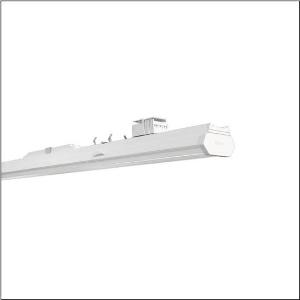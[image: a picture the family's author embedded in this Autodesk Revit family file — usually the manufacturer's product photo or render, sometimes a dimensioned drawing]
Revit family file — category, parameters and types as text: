
# Revit family: licross_r__11_protected_mo_51tp12cn58xf_fcc9
name_source: partatom
category: Lighting Fixtures
units: mm (PartAtom-declared; Revit-internal decimal feet)

## family parameters
Cut with Voids When Loaded = No
Host = Face
Light Source = No
Part Type = Normal
Room Calculation Point = No
Round Connector Dimension = Use Diameter
Shared = No

## types (1)
- --- (1 x LED, 8190 lm, 49 W, 5000K)
    Apparent Load = 49 VA
    CIE Flux Codes = 73 92 98 99 100
    Color Rendering = 80
    Color Temperature = 5000K
    Default Elevation = 1800 mm
    Description = Licross® 11 Protected MO, luminaire insert, of sheet steel, galvanised, coil coated, white, length: 1.500mm, width: 90mm, height: 101mm, LED rated luminous flux: 8.190lm, light colour: 850, control gear: ON/OFF Multilumen, CLOi, control gear: ECG Multilumen, with plug, 3-pole, with phase selection, mains connection: 220..240V, AC, 50/60Hz, start of lifetime: 49W, end of service life: 54W, halogen-free wiring, primary optical cover: cover, of PMMA, light emission: direct distribution, primary light characteristic: symmetric, protection rating (complete): IP64, insulation class (complete): insulation class I (protective earthing), certification: CE, ENEC, VDE, UKCA, protection symbol: D if used in an environment with conductive dust loads with corresponding accessories, impact resistance: IK06, permissible ambient temperature for indoor applications: -35..+40°C, reducing of maximum allowable ambient temperature of 5°C with ceiling mounting, corresponds to IFS (International Featured Standards) requirements for safety and quality in the food industry, LABS conformity tested according to VDMA 24364:2018-05, packaging unit: 1 piece
    Height = 92 mm
    Lamp = 1 x LED
    Lamp Light Flux = 8190 lm
    Lamp Power = 49 W
    Lamp count = 1
    Length = 1500 mm
    Luminous efficacy = 167 lm/W
    Manufacturer = Siteco
    ModVariant = No
    Model = 51TP12CN58XF
    Mounting Place = Ceiling
    Mounting Type = Pendant
    Number of Poles = 1
    OnlyDefault = Yes
    Power Factor = 1
    Product Name = Licross® 11 Protected MO
    Product group = luminaire insert
    ProductGroupID = 901
    Protection Class = Protection class I
    Protection Degree = IP 64
    RLX_Detail_Level = 1
    RLX_Emergency_Light_Flux = 0 lm
    RLX_Emergency_Type = 0
    RLX_Emergency_Type_DB = No
    RlxData = <blob elided: 22037 chars, md5=b464fee4>
    Socket = socket
    Standby Power = 0 W
    System Light Flux = 8190 lm
    System Power = 49 W
    Type Comments = factory setting: luminous flux: 100 % | (A | C | E) | 111 mA
    Type Image = l_1256148.jpg
    URL = http://relux.com
    VarID = @adj_158227
    Voltage = 0 V
    Weight = 0.00 kg
    Width = 88 mm

## geometry (parser evidence)
native form markers: Blend x4, Sweep x12
no freeform markers — native parametric forms only
